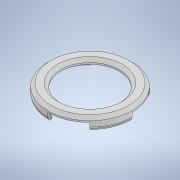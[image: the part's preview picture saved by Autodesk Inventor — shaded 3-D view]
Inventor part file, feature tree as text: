
AUTODESK INVENTOR PART (.ipt)
format: ipt  version: 2020 (Build 240168000, 168)  size: 196,608 bytes
history: native  units: mm
features: revolve x2, chamfer x2, sketch x2, other x1, pattern_circular x1
ambient origin geometry x8: Origin, YZ Plane, XZ Plane, XY Plane, X Axis, Y Axis, Z Axis, Center Point
bodies: Body1 (feature_tree)
feature tree (8):
  other  "Твердое тело1"
  revolve  "Вращение1"
  chamfer  "Фаска1"  Distance=19.0mm
  chamfer  "Фаска2"  Distance=27.3mm
  revolve  "Вращение2"
  pattern_circular  "Круговой массив1"  [2 undecoded]
  sketch  "Эскиз1"
  sketch  "Эскиз2"
note: 2 required parameter values undecoded (feature->parameter linkage not recoverable at this tier; creation-order binding heuristic only, values carry confidence <= 0.55)
